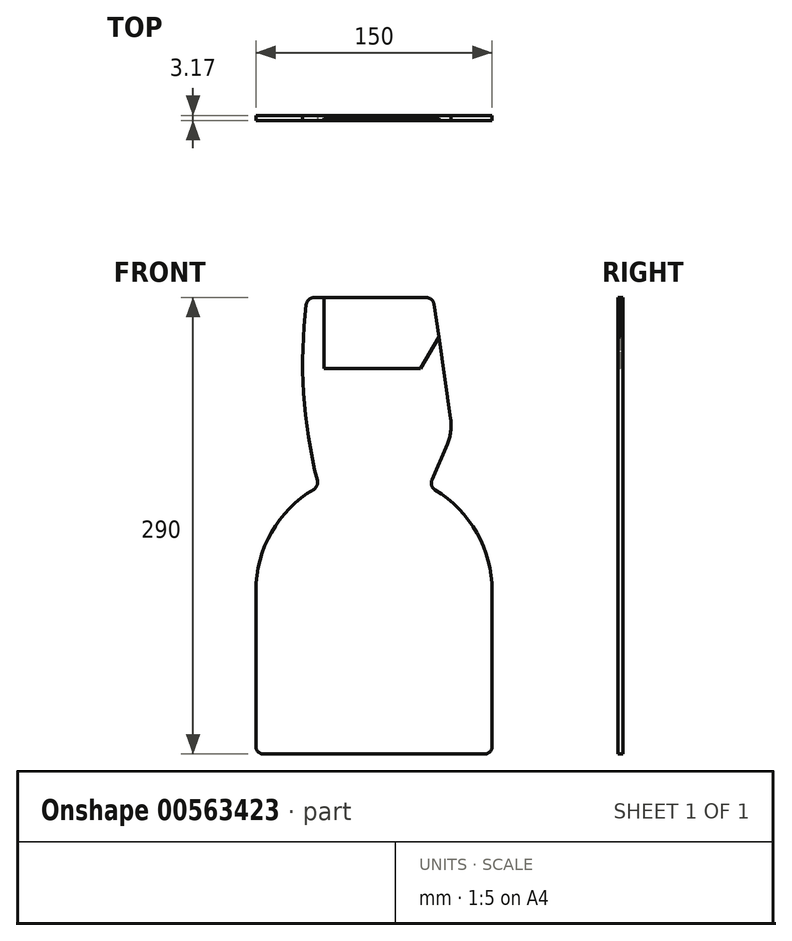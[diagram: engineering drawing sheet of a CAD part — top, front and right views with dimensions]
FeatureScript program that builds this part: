
annotation { "Feature Type Name" : "Feature", "Feature Type Description" : "" }
export const myFeature = defineFeature(function(context is Context, id is Id, definition is map)
    precondition{}
    {
        {
            var Q0;
            Q0=qCreatedBy(makeId("Front.planeOp"),FACE);
            var sketch = newSketch(context, id + "F0", { "sketchPlane" : qUnion([Q0])});
            skLineSegment(sketch, "E0", {"start": v(-75, 0) * mm, "end": v(75, 0) * mm});
            skLineSegment(sketch, "E1", {"start": v(-75, 0) * mm, "end": v(-75, 103.67) * mm});
            skArc(sketch, "E2", {"start": v(-35, 170) * mm, "mid": v(-64.23, 142.4) * mm, "end": v(-75, 103.67) * mm});
            skPoint(sketch, "E3", {"position": v(0, 0) * mm});
            skLineSegment(sketch, "E4", {"start": v(0, -46.41) * mm, "end": v(0, 246.59) * mm, "construction": true});
            skArc(sketch, "E5.MirrorCS", {"start": v(35, 170) * mm, "mid": v(64.23, 142.4) * mm, "end": v(75, 103.67) * mm});
            skLineSegment(sketch, "E6.MirrorCS", {"start": v(75, 0) * mm, "end": v(75, 103.67) * mm});
            skLineSegment(sketch, "E7", {"start": v(-42.48, 290) * mm, "end": v(37.52, 290) * mm});
            skLineSegment(sketch, "E8", {"start": v(37.52, 290) * mm, "end": v(49.9, 204.64) * mm});
            skLineSegment(sketch, "E9", {"start": v(49.9, 204.64) * mm, "end": v(35, 170) * mm});
            skArc(sketch, "E10", {"start": v(-42.48, 290) * mm, "mid": v(-44.76, 229.62) * mm, "end": v(-35, 170) * mm});
            skSolve(sketch);
        }
        {
            var Q0;
            Q0=makeQuery(id+"F0.imprint","IMPRINT",FACE,{"disambiguationData":[TD([[makeQuery(id+"F0.imprint","IMPRINT",EDGE,{"derivedFrom":sQuery(id+"F0.wireOp",EDGE,"E0")}),1.0]])]});
            extrude(context, id + "F1", {"entities" : qUnion([Q0]), "depth" : 3.17 * mm, "offsetDistance" : 25 * mm});
        }
        {
            var Q0;
            Q0=makeQuery(id+"F1.opExtrude","SWEPT_EDGE",EDGE,{"disambiguationData":[OSD([sQuery(id+"F0.wireOp",EDGE,"E2"),sQuery(id+"F0.wireOp",EDGE,"E10")])]});
            var Q1;
            Q1=makeQuery(id+"F1.opExtrude","SWEPT_EDGE",EDGE,{"disambiguationData":[OSD([sQuery(id+"F0.wireOp",EDGE,"E7"),sQuery(id+"F0.wireOp",EDGE,"E10")])]});
            var Q2;
            Q2=makeQuery(id+"F1.opExtrude","SWEPT_EDGE",EDGE,{"disambiguationData":[OSD([sQuery(id+"F0.wireOp",EDGE,"E7"),sQuery(id+"F0.wireOp",EDGE,"E8")])]});
            var Q3;
            Q3=makeQuery(id+"F1.opExtrude","SWEPT_EDGE",EDGE,{"disambiguationData":[OSD([sQuery(id+"F0.wireOp",EDGE,"E0"),sQuery(id+"F0.wireOp",EDGE,"E6.MirrorCS")])]});
            var Q4;
            Q4=makeQuery(id+"F1.opExtrude","SWEPT_EDGE",EDGE,{"disambiguationData":[OSD([sQuery(id+"F0.wireOp",EDGE,"E0"),sQuery(id+"F0.wireOp",EDGE,"E1")])]});
            var Q5;
            Q5=makeQuery(id+"F1.opExtrude","SWEPT_EDGE",EDGE,{"disambiguationData":[OSD([sQuery(id+"F0.wireOp",EDGE,"E5.MirrorCS"),sQuery(id+"F0.wireOp",EDGE,"E9")])]});
            fillet(context, id + "F2", {"entities" : qUnion([Q0, Q1, Q2, Q3, Q4, Q5]), "radius" : 5 * mm, "tangentPropagation" : true, "allowEdgeOverflow" : false});
        }
        {
            var Q0;
            Q0=makeQuery(id+"F1.opExtrude","SWEPT_EDGE",EDGE,{"disambiguationData":[OSD([sQuery(id+"F0.wireOp",EDGE,"E8"),sQuery(id+"F0.wireOp",EDGE,"E9")])]});
            fillet(context, id + "F3", {"entities" : qUnion([Q0]), "radius" : 30 * mm, "tangentPropagation" : true, "allowEdgeOverflow" : false});
        }
        {
            var Q0;
            Q0=makeQuery(id+"F1.opExtrude","CAP_FACE",FACE,{"disambiguationData":[OSD([sQuery(id+"F0.wireOp",EDGE,"E0"),sQuery(id+"F0.wireOp",EDGE,"E1"),sQuery(id+"F0.wireOp",EDGE,"E2"),sQuery(id+"F0.wireOp",EDGE,"E5.MirrorCS"),sQuery(id+"F0.wireOp",EDGE,"E6.MirrorCS"),sQuery(id+"F0.wireOp",EDGE,"E7"),sQuery(id+"F0.wireOp",EDGE,"E8"),sQuery(id+"F0.wireOp",EDGE,"E9"),sQuery(id+"F0.wireOp",EDGE,"E10")])],"isStart":false});
            var sketch = newSketch(context, id + "F4", { "sketchPlane" : qUnion([Q0])});
            skLineSegment(sketch, "E11", {"start": v(-31.66, 290) * mm, "end": v(-31.66, 245) * mm});
            skLineSegment(sketch, "E12", {"start": v(-31.66, 245) * mm, "end": v(29.6, 245) * mm});
            skLineSegment(sketch, "E13", {"start": v(29.6, 245) * mm, "end": v(41.14, 265) * mm});
            skLineSegment(sketch, "E14", {"start": v(41.14, 265) * mm, "end": v(41.14, 290) * mm});
            skLineSegment(sketch, "E15", {"start": v(41.14, 290) * mm, "end": v(-31.66, 290) * mm});
            skSolve(sketch);
        }
        {
            var Q0;
            {var subQ5=sQuery(id+"F4.wireOp",EDGE,"E11");Q0=makeQuery(id+"F4.imprint","IMPRINT",FACE,{"disambiguationData":[TD([[makeQuery(id+"F4.imprint","IMPRINT",EDGE,{"derivedFrom":subQ5}),1.0]])]});}
            extrude(context, id + "F5", {"entities" : qUnion([Q0]), "operationType" : NewBodyOperationType.REMOVE, "oppositeDirection" : true, "depth" : (3.17 / 2) * mm, "offsetDistance" : 25 * mm});
        }
    });
